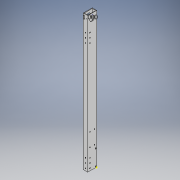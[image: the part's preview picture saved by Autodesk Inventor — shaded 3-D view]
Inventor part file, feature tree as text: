
AUTODESK INVENTOR PART (.ipt)
format: ipt  version: 2018 (Build 220112000, 112)  size: 209,920 bytes
history: native  units: in
note: dims shown in document units (in); Inventor stores cm internally (conversion verified against a paired STEP export)
features: sketch x7, extrude x6
ambient origin geometry x8: Origin, YZ Plane, XZ Plane, XY Plane, X Axis, Y Axis, Z Axis, Center Point
bodies: Solid1 (feature_tree)
feature tree (13):
  extrude  "Extrusion1"  Depth=2.0in
  extrude  "Extrusion3"  Depth=30.0in TaperAngle=0.0deg
  sketch  "Sketch4"  dims[d19=0.5in d20=1.0in]
  extrude  "Extrusion4"  Depth=1.0in
  extrude  "Extrusion5"  Depth=1.0in
  extrude  "Extrusion6"  Depth=0.2031in
  extrude  "Extrusion7"  Depth=30.0in
  sketch  "Sketch1"  dims[d0=1.0in d1=2.0in]
  sketch  "Sketch3"  dims[d2=0.125in d3=30.0in d4=0.0in]
  sketch  "Sketch5"  dims[d21=1.0in d22=0.2031in]
  sketch  "Sketch6"  dims[d23=0.2031in d24=0.2031in]
  sketch  "Sketch7"  dims[d30=30.0in d31=0.0in d38=0.5in]
  sketch  "Sketch8"  dims[d39=0.2031in d40=1.0in d41=1.0in d42=0.2031in d43=0.2031in d44=1.0in d46=0.5in d47=0.5in d48=0.2031in d49=0.2031in d50=0.2031in d51=0.5in d52=0.5in d53=0.5in d54=0.2031in d55=0.2031in d56=0.2031in d57=30.0in d58=0.0in d59=1.0in d60=1.125in d61=12.0in d62=0.0in d63=4.0in d64=7.0in d65=1.0in d66=1.0in d67=0.2031in d68=0.2031in d69=0.2031in d70=0.2031in d71=2.0in d72=0.0in d73=0.256in d74=0.256in d75=0.26in d76=3.425in d77=0.26in d78=2.0in d79=0.0in]
